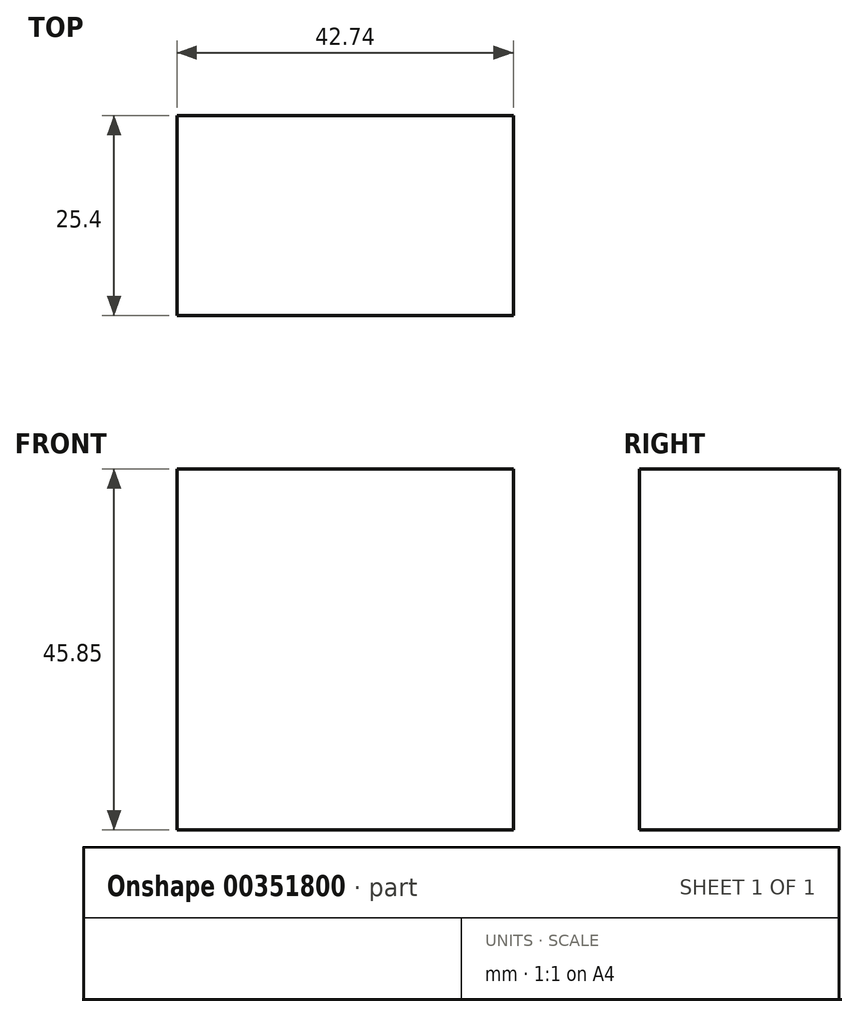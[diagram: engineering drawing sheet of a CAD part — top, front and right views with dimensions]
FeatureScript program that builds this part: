
annotation { "Feature Type Name" : "Feature", "Feature Type Description" : "" }
export const myFeature = defineFeature(function(context is Context, id is Id, definition is map)
    precondition{}
    {
        {
            var Q0;
            Q0=qCreatedBy(makeId("Front.planeOp"),FACE);
            var sketch = newSketch(context, id + "F0", { "sketchPlane" : qUnion([Q0])});
            skLineSegment(sketch, "E0", {"start": v(0, 0) * mm, "end": v(0, 45.85) * mm});
            skLineSegment(sketch, "E1", {"start": v(0, 45.85) * mm, "end": v(42.74, 45.85) * mm});
            skLineSegment(sketch, "E2", {"start": v(42.74, 45.85) * mm, "end": v(42.74, 0) * mm});
            skLineSegment(sketch, "E3", {"start": v(42.74, 0) * mm, "end": v(0, 0) * mm});
            skSolve(sketch);
        }
        {
            var Q0;
            Q0 = qSketchRegion(id + "F0", true);
            extrude(context, id + "F1", {"entities" : qUnion([Q0]), "depth" : 25.4 * mm});
        }
    });
